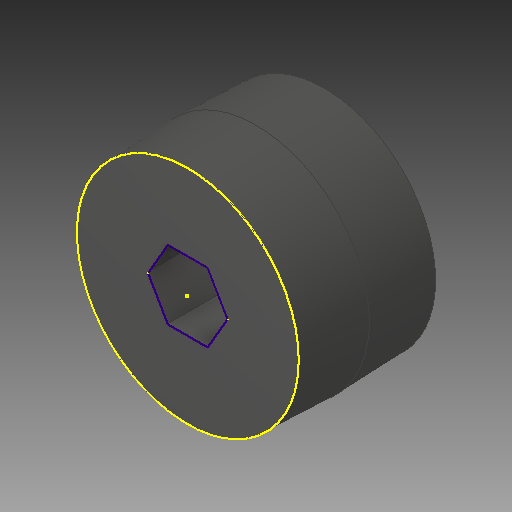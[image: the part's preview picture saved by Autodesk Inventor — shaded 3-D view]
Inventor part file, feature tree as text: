
AUTODESK INVENTOR PART (.ipt)
format: ipt  version: 2017 (Build 210142000, 142)  size: 688,128 bytes
history: native  units: in
note: dims shown in document units (in); Inventor stores cm internally (conversion verified against a paired STEP export)
features: sketch x1, projected_geometry x1, other x1
ambient origin geometry x8: Origin, YZ Plane, XZ Plane, XY Plane, X Axis, Y Axis, Z Axis, Center Point
bodies: Solid1 (feature_tree)
feature tree (3):
  sketch  "Sketch1"
  projected_geometry  "Projected Loop1"
  other  "_2in Wheel Intergrated Hub Design_-_CirPattern1_"
